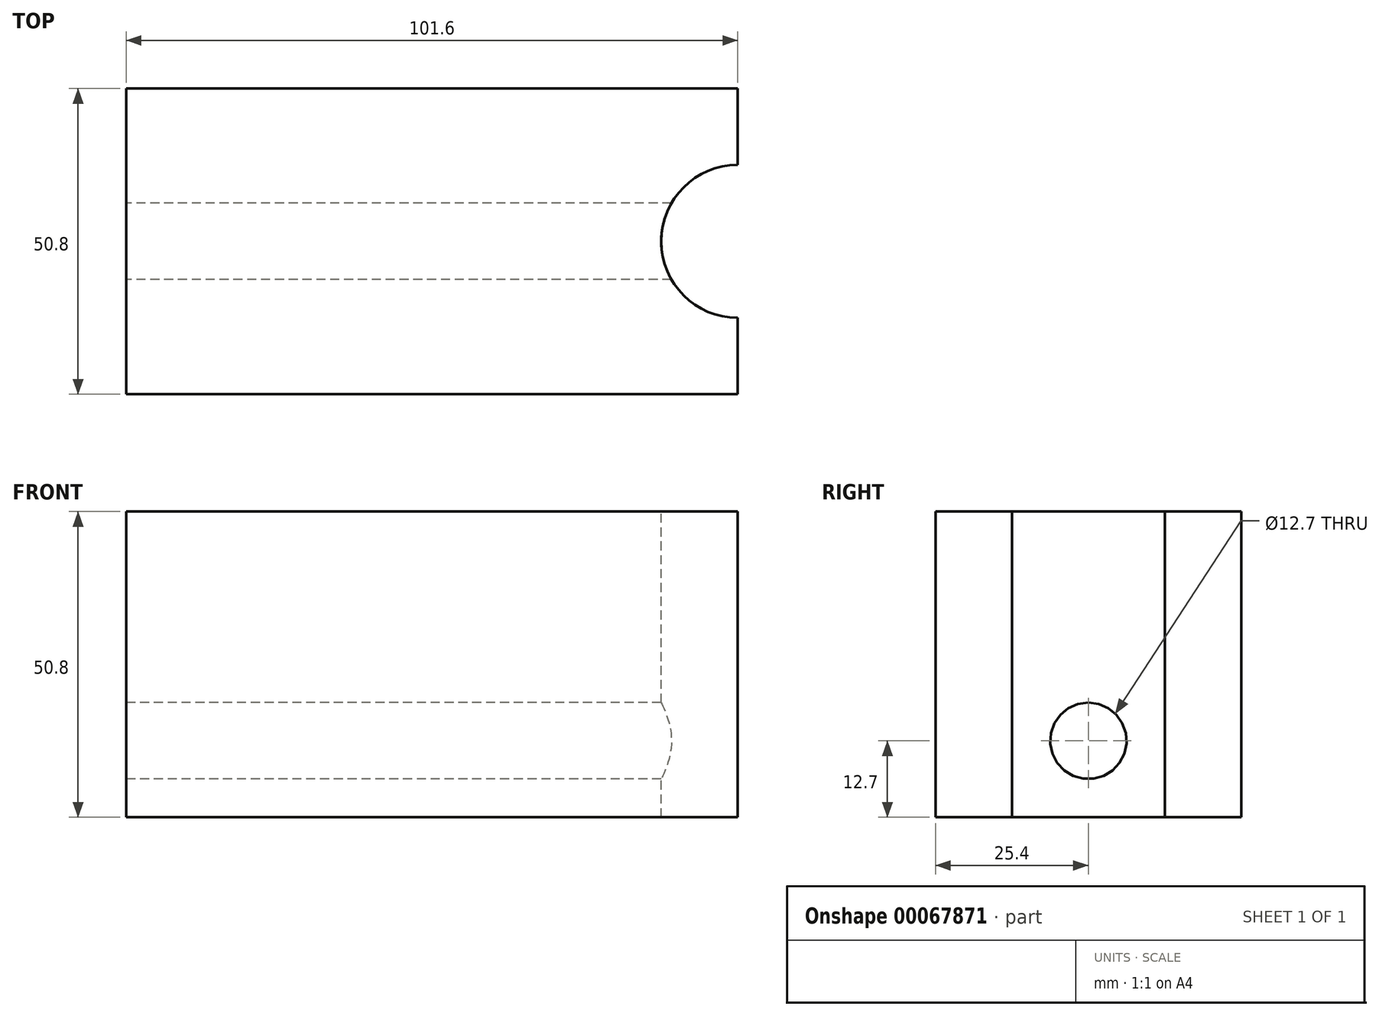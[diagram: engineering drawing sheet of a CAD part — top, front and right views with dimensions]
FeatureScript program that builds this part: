
annotation { "Feature Type Name" : "Feature", "Feature Type Description" : "" }
export const myFeature = defineFeature(function(context is Context, id is Id, definition is map)
    precondition{}
    {
        {
            var Q0;
            Q0=qCreatedBy(makeId("Top.planeOp"),FACE);
            var sketch = newSketch(context, id + "F0", { "sketchPlane" : qUnion([Q0])});
            skLineSegment(sketch, "E0.bottom", {"start": v(0, 0) * mm, "end": v(101.6, 0) * mm});
            skLineSegment(sketch, "E0.top", {"start": v(0, 50.8) * mm, "end": v(101.6, 50.8) * mm});
            skLineSegment(sketch, "E0.left", {"start": v(0, 0) * mm, "end": v(0, 50.8) * mm});
            skLineSegment(sketch, "E0.right", {"start": v(101.6, 0) * mm, "end": v(101.6, 50.8) * mm});
            skSolve(sketch);
        }
        {
            var Q0;
            Q0=makeQuery(id+"F0.imprint","IMPRINT",FACE,{"disambiguationData":[TD([[makeQuery(id+"F0.imprint","IMPRINT",EDGE,{"derivedFrom":sQuery(id+"F0.wireOp",EDGE,"E0.bottom")}),1.0]])]});
            extrude(context, id + "F1", {"entities" : qUnion([Q0]), "depth" : 50.8 * mm});
        }
        {
            var Q0;
            Q0=makeQuery(id+"F1.opExtrude","CAP_FACE",FACE,{"disambiguationData":[OSD([sQuery(id+"F0.wireOp",EDGE,"E0.bottom"),sQuery(id+"F0.wireOp",EDGE,"E0.top"),sQuery(id+"F0.wireOp",EDGE,"E0.left"),sQuery(id+"F0.wireOp",EDGE,"E0.right")])],"isStart":false});
            var sketch = newSketch(context, id + "F2", { "sketchPlane" : qUnion([Q0])});
            skCircle(sketch, "E1", {"center": v(101.6, 25.4) * mm, "radius": 12.7 * mm});
            skSolve(sketch);
        }
        {
            var Q0;
            {var subQ0=sQuery(id+"F2.wireOp",EDGE,"E1");var subQ1=makeQuery(id+"F1.opExtrude","CAP_EDGE",EDGE,{"disambiguationData":[OSD([sQuery(id+"F0.wireOp",EDGE,"E0.right")])],"isStart":false});var subQ2=makeQuery(id+"F2.imprint","INTERSECT",VERTEX,{"disambiguationData":[OD(0.0)],"derivedFrom":[subQ1,subQ0]});Q0=makeQuery(id+"F2.imprint","IMPRINT",FACE,{"disambiguationData":[TD([[makeQuery(id+"F2.imprint","IMPRINT",EDGE,{"disambiguationData":[TD([[subQ2,1.0]])],"derivedFrom":subQ0}),1.0]])]});}
            extrude(context, id + "F3", {"entities" : qUnion([Q0]), "operationType" : NewBodyOperationType.REMOVE, "endBound" : BoundingType.THROUGH_ALL, "oppositeDirection" : true, "depth" : 25.4 * mm});
        }
        {
            var Q0;
            Q0=makeQuery(id+"F1.opExtrude","SWEPT_FACE",FACE,{"disambiguationData":[OSD([sQuery(id+"F0.wireOp",EDGE,"E0.left")])]});
            var sketch = newSketch(context, id + "F4", { "sketchPlane" : qUnion([Q0])});
            skLineSegment(sketch, "E2", {"start": v(-25.4, 0) * mm, "end": v(-25.4, 50.8) * mm, "construction": true});
            skCircle(sketch, "E3", {"center": v(-25.4, 12.7) * mm, "radius": 6.35 * mm});
            skSolve(sketch);
        }
        {
            var Q0;
            Q0=makeQuery(id+"F4.imprint","IMPRINT",FACE,{"disambiguationData":[TD([[makeQuery(id+"F4.imprint","IMPRINT",EDGE,{"derivedFrom":sQuery(id+"F4.wireOp",EDGE,"E3")}),1.0]])]});
            extrude(context, id + "F5", {"entities" : qUnion([Q0]), "operationType" : NewBodyOperationType.REMOVE, "endBound" : BoundingType.THROUGH_ALL, "oppositeDirection" : true, "depth" : 25.4 * mm});
        }
    });
